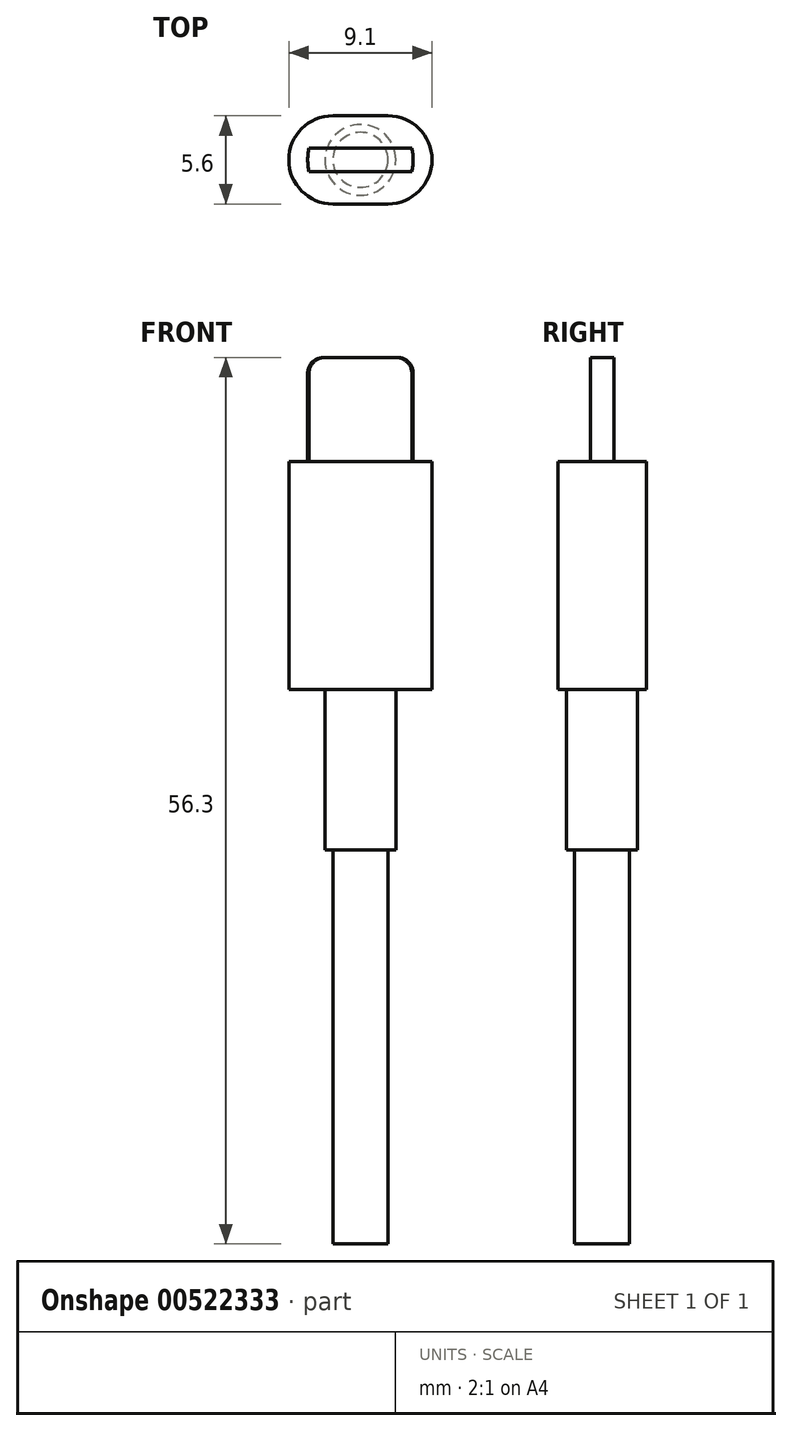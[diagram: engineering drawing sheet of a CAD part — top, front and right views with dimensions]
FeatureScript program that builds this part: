
annotation { "Feature Type Name" : "Feature", "Feature Type Description" : "" }
export const myFeature = defineFeature(function(context is Context, id is Id, definition is map)
    precondition{}
    {
        {
            var Q0;
            Q0=qCreatedBy(makeId("Top.planeOp"),FACE);
            var sketch = newSketch(context, id + "F0", { "sketchPlane" : qUnion([Q0])});
            skLineSegment(sketch, "E0.bottom", {"start": v(1.75, 2.8) * mm, "end": v(-1.75, 2.8) * mm});
            skLineSegment(sketch, "E0.top", {"start": v(1.75, -2.8) * mm, "end": v(-1.75, -2.8) * mm});
            skPoint(sketch, "E0.middle", {"position": v(0, 0) * mm});
            skArc(sketch, "E1", {"start": v(-1.75, 2.8) * mm, "mid": v(-4.55, 0) * mm, "end": v(-1.75, -2.8) * mm});
            skArc(sketch, "E2", {"start": v(1.75, 2.8) * mm, "mid": v(4.55, 0) * mm, "end": v(1.75, -2.8) * mm});
            skLineSegment(sketch, "E3", {"start": v(0, 0) * mm, "end": v(0, 2.8) * mm, "construction": true});
            skSolve(sketch);
        }
        {
            var Q0;
            Q0 = qSketchRegion(id + "F0", true);
            extrude(context, id + "F1", {"entities" : qUnion([Q0]), "depth" : 14.5 * mm, "offsetDistance" : 25 * mm});
        }
        {
            var Q0;
            Q0=makeQuery(id+"F1.opExtrude","CAP_FACE",FACE,{"disambiguationData":[OSD([sQuery(id+"F0.wireOp",EDGE,"E0.bottom"),sQuery(id+"F0.wireOp",EDGE,"E0.top"),sQuery(id+"F0.wireOp",EDGE,"E1"),sQuery(id+"F0.wireOp",EDGE,"E2")])],"isStart":false});
            var sketch = newSketch(context, id + "F2", { "sketchPlane" : qUnion([Q0])});
            skArc(sketch, "E4", {"start": v(-3.26, 0.75) * mm, "mid": v(-3.35, 0) * mm, "end": v(-3.26, -0.75) * mm});
            skLineSegment(sketch, "E5", {"start": v(-3.26, 0.75) * mm, "end": v(3.26, 0.75) * mm});
            skLineSegment(sketch, "E6", {"start": v(-3.26, -0.75) * mm, "end": v(3.26, -0.75) * mm});
            skLineSegment(sketch, "E7", {"start": v(0, 0) * mm, "end": v(-8.5, 0) * mm, "construction": true});
            skArc(sketch, "E8.trimOffspring", {"start": v(3.26, -0.75) * mm, "mid": v(3.35, 0) * mm, "end": v(3.26, 0.75) * mm});
            skSolve(sketch);
        }
        {
            var Q0;
            Q0 = qSketchRegion(id + "F2", true);
            extrude(context, id + "F3", {"entities" : qUnion([Q0]), "operationType" : NewBodyOperationType.ADD, "depth" : 6.6 * mm, "offsetDistance" : 25 * mm});
        }
        {
            var Q0;
            Q0=makeQuery(id+"F3.opExtrude","CAP_EDGE",EDGE,{"disambiguationData":[OSD([sQuery(id+"F2.wireOp",EDGE,"E4")])],"isStart":false});
            var Q1;
            Q1=makeQuery(id+"F3.opExtrude","CAP_EDGE",EDGE,{"disambiguationData":[OSD([sQuery(id+"F2.wireOp",EDGE,"E8.trimOffspring")])],"isStart":false});
            fillet(context, id + "F4", {"entities" : qUnion([Q0, Q1]), "radius" : 1 * mm, "tangentPropagation" : true, "allowEdgeOverflow" : false});
        }
        {
            var Q0;
            Q0=makeQuery(id+"F1.opExtrude","CAP_FACE",FACE,{"disambiguationData":[OSD([sQuery(id+"F0.wireOp",EDGE,"E0.bottom"),sQuery(id+"F0.wireOp",EDGE,"E0.top"),sQuery(id+"F0.wireOp",EDGE,"E1"),sQuery(id+"F0.wireOp",EDGE,"E2")])],"isStart":true});
            var sketch = newSketch(context, id + "F5", { "sketchPlane" : qUnion([Q0])});
            skCircle(sketch, "E9", {"center": v(0, 0) * mm, "radius": 2.25 * mm});
            skSolve(sketch);
        }
        {
            var Q0;
            Q0 = qSketchRegion(id + "F5", true);
            extrude(context, id + "F6", {"entities" : qUnion([Q0]), "operationType" : NewBodyOperationType.ADD, "depth" : 10.2 * mm, "offsetDistance" : 25 * mm});
        }
        {
            var Q0;
            Q0=makeQuery(id+"F6.opExtrude","CAP_FACE",FACE,{"disambiguationData":[OSD([sQuery(id+"F5.wireOp",EDGE,"E9")])],"isStart":false});
            var sketch = newSketch(context, id + "F7", { "sketchPlane" : qUnion([Q0])});
            skCircle(sketch, "E10", {"center": v(0, 0) * mm, "radius": 1.75 * mm});
            skSolve(sketch);
        }
        {
            var Q0;
            Q0 = qSketchRegion(id + "F7", true);
            extrude(context, id + "F8", {"entities" : qUnion([Q0]), "operationType" : NewBodyOperationType.ADD, "depth" : 25 * mm, "offsetDistance" : 25 * mm});
        }
    });
